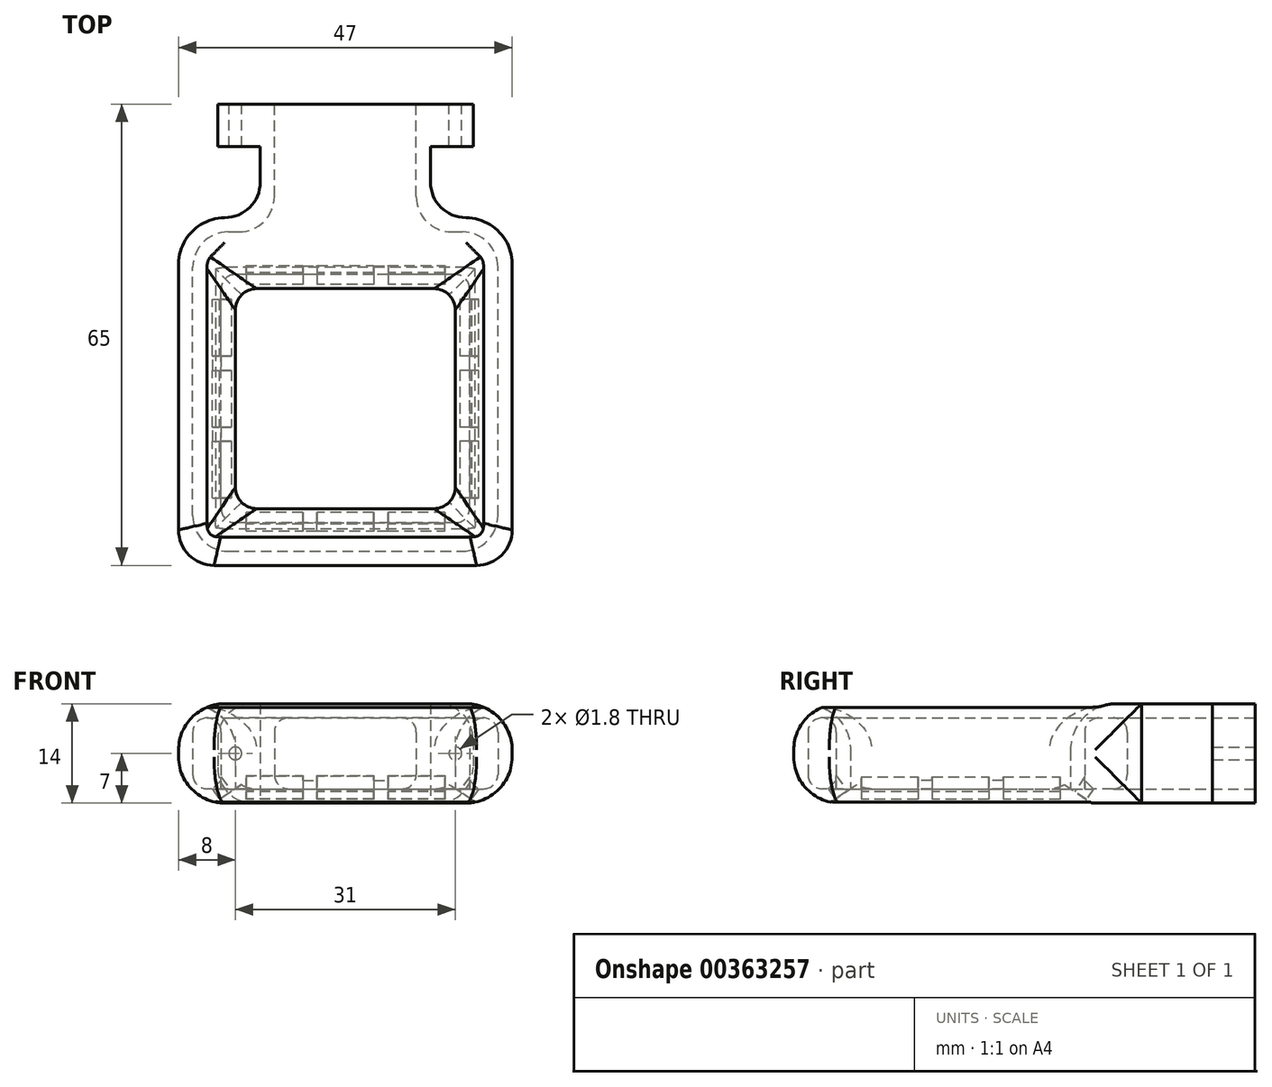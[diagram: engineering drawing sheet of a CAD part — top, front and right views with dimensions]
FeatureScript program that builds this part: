
annotation { "Feature Type Name" : "Feature", "Feature Type Description" : "" }
export const myFeature = defineFeature(function(context is Context, id is Id, definition is map)
    precondition{}
    {
        {
            var Q0;
            Q0=qCreatedBy(makeId("Top.planeOp"),FACE);
            var sketch = newSketch(context, id + "F0", { "sketchPlane" : qUnion([Q0])});
            skLineSegment(sketch, "E0.bottom", {"start": v(-12, 24.5) * mm, "end": v(12, 24.5) * mm});
            skLineSegment(sketch, "E0.top", {"start": v(-12, 40.5) * mm, "end": v(12, 40.5) * mm});
            skLineSegment(sketch, "E0.left", {"start": v(-12, 24.5) * mm, "end": v(-12, 40.5) * mm});
            skLineSegment(sketch, "E0.right", {"start": v(12, 24.5) * mm, "end": v(12, 40.5) * mm});
            skLineSegment(sketch, "E1.bottom", {"start": v(-23.5, -24.5) * mm, "end": v(23.5, -24.5) * mm});
            skLineSegment(sketch, "E1.top", {"start": v(-23.5, 24.5) * mm, "end": v(23.5, 24.5) * mm});
            skLineSegment(sketch, "E1.left", {"start": v(-23.5, -24.5) * mm, "end": v(-23.5, 24.5) * mm});
            skLineSegment(sketch, "E1.right", {"start": v(23.5, -24.5) * mm, "end": v(23.5, 24.5) * mm});
            skPoint(sketch, "E2", {"position": v(0, 24.5) * mm});
            skLineSegment(sketch, "E3.bottom", {"start": v(15.5, -16.5) * mm, "end": v(-15.5, -16.5) * mm});
            skLineSegment(sketch, "E3.top", {"start": v(15.5, 14.5) * mm, "end": v(-15.5, 14.5) * mm});
            skLineSegment(sketch, "E3.left", {"start": v(15.5, -16.5) * mm, "end": v(15.5, 14.5) * mm});
            skLineSegment(sketch, "E3.right", {"start": v(-15.5, -16.5) * mm, "end": v(-15.5, 14.5) * mm});
            skPoint(sketch, "E3.middle", {"position": v(0, 0) * mm});
            skPoint(sketch, "E4", {"position": v(-23.5, 0) * mm});
            skSolve(sketch);
        }
        {
            var Q0;
            Q0=qSketchRegion(id+"F0",true);
            extrude(context, id + "F1", {"entities" : qUnion([Q0]), "depth" : 14 * mm});
        }
        {
            var Q0;
            Q0=makeQuery(id+"F1.opExtrude","SWEPT_FACE",FACE,{"disambiguationData":[OSD([sQuery(id+"F0.wireOp",EDGE,"E0.top")])]});
            shell(context, id + "F2", {"entities" : qUnion([Q0]), "thickness" : 2 * mm});
        }
        {
            var Q0;
            Q0=makeQuery(id+"F1.opExtrude","SWEPT_FACE",FACE,{"disambiguationData":[OSD([sQuery(id+"F0.wireOp",EDGE,"E0.right")])]});
            var sketch = newSketch(context, id + "F3", { "sketchPlane" : qUnion([Q0])});
            skLineSegment(sketch, "E5.bottom", {"start": v(40.5, 14) * mm, "end": v(34.5, 14) * mm});
            skLineSegment(sketch, "E5.top", {"start": v(40.5, 0) * mm, "end": v(34.5, 0) * mm});
            skLineSegment(sketch, "E5.left", {"start": v(40.5, 14) * mm, "end": v(40.5, 0) * mm});
            skLineSegment(sketch, "E5.right", {"start": v(34.5, 14) * mm, "end": v(34.5, 0) * mm});
            skSolve(sketch);
        }
        {
            var Q0;
            Q0=makeQuery(id+"F3.imprint","IMPRINT",FACE,{"disambiguationData":[TD([[makeQuery(id+"F3.imprint","IMPRINT",EDGE,{"derivedFrom":sQuery(id+"F3.wireOp",EDGE,"E5.bottom")}),-1.0]])]});
            extrude(context, id + "F4", {"entities" : qUnion([Q0]), "operationType" : NewBodyOperationType.ADD, "depth" : 6 * mm});
        }
        {
            var Q0;
            Q0=makeQuery(id+"F1.opExtrude","SWEPT_FACE",FACE,{"disambiguationData":[OSD([sQuery(id+"F0.wireOp",EDGE,"E0.left")])]});
            var sketch = newSketch(context, id + "F5", { "sketchPlane" : qUnion([Q0])});
            skLineSegment(sketch, "E6.bottom", {"start": v(-40.5, 14) * mm, "end": v(-34.5, 14) * mm});
            skLineSegment(sketch, "E6.top", {"start": v(-40.5, 0) * mm, "end": v(-34.5, 0) * mm});
            skLineSegment(sketch, "E6.left", {"start": v(-40.5, 14) * mm, "end": v(-40.5, 0) * mm});
            skLineSegment(sketch, "E6.right", {"start": v(-34.5, 14) * mm, "end": v(-34.5, 0) * mm});
            skSolve(sketch);
        }
        {
            var Q0;
            Q0=makeQuery(id+"F5.imprint","IMPRINT",FACE,{"disambiguationData":[TD([[makeQuery(id+"F5.imprint","IMPRINT",EDGE,{"derivedFrom":sQuery(id+"F5.wireOp",EDGE,"E6.bottom")}),1.0]])]});
            extrude(context, id + "F6", {"entities" : qUnion([Q0]), "operationType" : NewBodyOperationType.ADD, "depth" : 6 * mm});
        }
        {
            var Q0;
            Q0=makeQuery(id+"F6.boolean.opBoolean","MERGE",FACE,{"derivedFrom":[makeQuery(id+"F4.boolean.opBoolean","MERGE",FACE,{"derivedFrom":[makeQuery(id+"FMbawrjq5tevXZs_1.boolean.opBoolean","MERGE",FACE,{"derivedFrom":[makeQuery(id+"F1.opExtrude","SWEPT_FACE",FACE,{"disambiguationData":[OSD([sQuery(id+"F0.wireOp",EDGE,"E0.top")])]}),makeQuery(id+"FMbawrjq5tevXZs_1.opExtrude","SWEPT_FACE",FACE,{"disambiguationData":[OSD([sQuery(id+"FMr8k5ix8z9LvOk_1.wireOp",EDGE,"X72l2WwN-p526-XuUv-XZvA-PvNH8UyjeKjB.left")])]})]}),makeQuery(id+"F4.opExtrude","SWEPT_FACE",FACE,{"disambiguationData":[OSD([sQuery(id+"F3.wireOp",EDGE,"E5.left")])]})]}),makeQuery(id+"F6.opExtrude","SWEPT_FACE",FACE,{"disambiguationData":[OSD([sQuery(id+"F5.wireOp",EDGE,"E6.left")])]})]});
            var sketch = newSketch(context, id + "F7", { "sketchPlane" : qUnion([Q0])});
            skCircle(sketch, "E7", {"center": v(-15.5, 7) * mm, "radius": 0.9 * mm});
            skCircle(sketch, "E8", {"center": v(15.5, 7) * mm, "radius": 0.9 * mm});
            skSolve(sketch);
        }
        {
            var Q0;
            Q0=makeQuery(id+"F4.opExtrude","CAP_EDGE",EDGE,{"disambiguationData":[OSD([sQuery(id+"F3.wireOp",EDGE,"E5.top")])],"isStart":false});
            var Q1;
            Q1=makeQuery(id+"F4.opExtrude","CAP_EDGE",EDGE,{"disambiguationData":[OSD([sQuery(id+"F3.wireOp",EDGE,"E5.bottom")])],"isStart":false});
            var Q2;
            Q2=makeQuery(id+"F6.opExtrude","CAP_EDGE",EDGE,{"disambiguationData":[OSD([sQuery(id+"F5.wireOp",EDGE,"E6.bottom")])],"isStart":false});
            var Q3;
            Q3=makeQuery(id+"F6.opExtrude","CAP_EDGE",EDGE,{"disambiguationData":[OSD([sQuery(id+"F5.wireOp",EDGE,"E6.top")])],"isStart":false});
            fillet(context, id + "F8", {"entities" : qUnion([Q0, Q1, Q2, Q3]), "radius" : 5 * mm, "tangentPropagation" : true, "allowEdgeOverflow" : false});
        }
        {
            var Q0;
            Q0=qSketchRegion(id+"F7",true);
            extrude(context, id + "F9", {"entities" : qUnion([Q0]), "operationType" : NewBodyOperationType.REMOVE, "endBound" : BoundingType.UP_TO_NEXT, "oppositeDirection" : true, "depth" : 25 * mm});
        }
        {
            var Q0;
            Q0=makeQuery(id+"F1.opExtrude","CAP_EDGE",EDGE,{"disambiguationData":[OSD([sQuery(id+"F0.wireOp",EDGE,"E3.right")])],"isStart":true});
            var Q1;
            Q1=makeQuery(id+"F1.opExtrude","CAP_EDGE",EDGE,{"disambiguationData":[OSD([sQuery(id+"F0.wireOp",EDGE,"E3.top")])],"isStart":true});
            var Q2;
            Q2=makeQuery(id+"F1.opExtrude","CAP_EDGE",EDGE,{"disambiguationData":[OSD([sQuery(id+"F0.wireOp",EDGE,"E3.bottom")])],"isStart":true});
            var Q3;
            Q3=makeQuery(id+"F1.opExtrude","CAP_EDGE",EDGE,{"disambiguationData":[OSD([sQuery(id+"F0.wireOp",EDGE,"E3.left")])],"isStart":true});
            chamfer(context, id + "F10", {"entities" : qUnion([Q0, Q1, Q2, Q3]), "chamferType" : ChamferType.TWO_OFFSETS, "width1" : 2 * mm, "oppositeDirection" : false, "width2" : 3 * mm, "tangentPropagation" : true});
        }
        {
            var Q0;
            Q0=makeQuery(id+"F1.opExtrude","CAP_EDGE",EDGE,{"disambiguationData":[OSD([sQuery(id+"F0.wireOp",EDGE,"E1.right")])],"isStart":false});
            var Q1;
            Q1=makeQuery(id+"F1.opExtrude","CAP_EDGE",EDGE,{"disambiguationData":[OSD([sQuery(id+"F0.wireOp",EDGE,"E1.right")])],"isStart":true});
            var Q2;
            Q2=makeQuery(id+"F1.opExtrude","SWEPT_EDGE",EDGE,{"disambiguationData":[OSD([sQuery(id+"F0.wireOp",EDGE,"E1.top"),sQuery(id+"F0.wireOp",EDGE,"E1.right")])]});
            var Q3;
            Q3=makeQuery(id+"F1.opExtrude","CAP_EDGE",EDGE,{"disambiguationData":[OSD([sQuery(id+"F0.wireOp",EDGE,"E1.bottom")])],"isStart":false});
            var Q4;
            Q4=makeQuery(id+"F1.opExtrude","CAP_EDGE",EDGE,{"disambiguationData":[OSD([sQuery(id+"F0.wireOp",EDGE,"E1.bottom")])],"isStart":true});
            var Q5;
            Q5=makeQuery(id+"F1.opExtrude","CAP_EDGE",EDGE,{"disambiguationData":[OSD([sQuery(id+"F0.wireOp",EDGE,"E1.left")])],"isStart":true});
            var Q6;
            Q6=makeQuery(id+"F1.opExtrude","CAP_EDGE",EDGE,{"disambiguationData":[OSD([sQuery(id+"F0.wireOp",EDGE,"E1.left")])],"isStart":false});
            var Q7;
            Q7=makeQuery(id+"F1.opExtrude","SWEPT_EDGE",EDGE,{"disambiguationData":[OSD([sQuery(id+"F0.wireOp",EDGE,"E1.top"),sQuery(id+"F0.wireOp",EDGE,"E1.left")])]});
            var Q8;
            Q8=makeQuery(id+"F1.opExtrude","CAP_EDGE",EDGE,{"disambiguationData":[OSD([sQuery(id+"F0.wireOp",EDGE,"E3.top")])],"isStart":false});
            var Q9;
            Q9=makeQuery(id+"F1.opExtrude","CAP_EDGE",EDGE,{"disambiguationData":[OSD([sQuery(id+"F0.wireOp",EDGE,"E3.right")])],"isStart":false});
            var Q10;
            Q10=makeQuery(id+"F1.opExtrude","CAP_EDGE",EDGE,{"disambiguationData":[OSD([sQuery(id+"F0.wireOp",EDGE,"E3.bottom")])],"isStart":false});
            var Q11;
            Q11=makeQuery(id+"F1.opExtrude","CAP_EDGE",EDGE,{"disambiguationData":[OSD([sQuery(id+"F0.wireOp",EDGE,"E3.left")])],"isStart":false});
            fillet(context, id + "F11", {"entities" : qUnion([Q0, Q1, Q2, Q3, Q4, Q5, Q6, Q7, Q8, Q9, Q10, Q11]), "radius" : 6.5 * mm, "tangentPropagation" : true, "allowEdgeOverflow" : false});
        }
        {
            var Q0;
            Q0=makeQuery(id+"F2.opShell","OFFSET_EDGE",EDGE,{"disambiguationData":[OSD([sQuery(id+"F0.wireOp",EDGE,"E1.top"),sQuery(id+"F0.wireOp",EDGE,"E1.right")])]});
            var Q1;
            Q1=makeQuery(id+"F2.opShell","OFFSET_EDGE",EDGE,{"disambiguationData":[OSD([sQuery(id+"F0.wireOp",EDGE,"E1.bottom"),sQuery(id+"F0.wireOp",EDGE,"E1.right")])]});
            var Q2;
            Q2=makeQuery(id+"F2.opShell","OFFSET_EDGE",EDGE,{"disambiguationData":[OSD([sQuery(id+"F0.wireOp",EDGE,"E1.bottom"),sQuery(id+"F0.wireOp",EDGE,"E1.left")])]});
            var Q3;
            Q3=makeQuery(id+"F2.opShell","OFFSET_EDGE",EDGE,{"disambiguationData":[OSD([sQuery(id+"F0.wireOp",EDGE,"E1.top"),sQuery(id+"F0.wireOp",EDGE,"E1.left")])]});
            var Q4;
            Q4=makeQuery(id+"F2.opShell","OFFSET_EDGE",EDGE,{"disambiguationData":[OSD([sQuery(id+"F0.wireOp",EDGE,"E0.left"),sQuery(id+"F0.wireOp",EDGE,"E1.top")])]});
            var Q5;
            Q5=makeQuery(id+"F2.opShell","OFFSET_EDGE",EDGE,{"disambiguationData":[OSD([sQuery(id+"F0.wireOp",EDGE,"E0.right"),sQuery(id+"F0.wireOp",EDGE,"E1.top")])]});
            var Q6;
            Q6=makeQuery(id+"F1.opExtrude","SWEPT_EDGE",EDGE,{"disambiguationData":[OSD([sQuery(id+"F0.wireOp",EDGE,"E0.right"),sQuery(id+"F0.wireOp",EDGE,"E1.top")])]});
            var Q7;
            Q7=makeQuery(id+"F1.opExtrude","SWEPT_EDGE",EDGE,{"disambiguationData":[OSD([sQuery(id+"F0.wireOp",EDGE,"E0.left"),sQuery(id+"F0.wireOp",EDGE,"E1.top")])]});
            var Q8;
            Q8=makeQuery(id+"F6.opExtrude","CAP_EDGE",EDGE,{"disambiguationData":[OSD([sQuery(id+"F5.wireOp",EDGE,"E6.right")])],"isStart":true});
            var Q9;
            Q9=makeQuery(id+"F4.opExtrude","CAP_EDGE",EDGE,{"disambiguationData":[OSD([sQuery(id+"F3.wireOp",EDGE,"E5.right")])],"isStart":true});
            fillet(context, id + "F12", {"entities" : qUnion([Q0, Q1, Q2, Q3, Q4, Q5, Q6, Q7, Q8, Q9]), "radius" : 5 * mm, "tangentPropagation" : true, "allowEdgeOverflow" : false});
        }
        {
            var Q0;
            Q0=makeQuery(id+"F1.opExtrude","SWEPT_EDGE",EDGE,{"disambiguationData":[OSD([sQuery(id+"F0.wireOp",EDGE,"E3.top"),sQuery(id+"F0.wireOp",EDGE,"E3.left")])]});
            var Q1;
            Q1=makeQuery(id+"F1.opExtrude","SWEPT_EDGE",EDGE,{"disambiguationData":[OSD([sQuery(id+"F0.wireOp",EDGE,"E3.bottom"),sQuery(id+"F0.wireOp",EDGE,"E3.left")])]});
            var Q2;
            Q2=makeQuery(id+"F1.opExtrude","SWEPT_EDGE",EDGE,{"disambiguationData":[OSD([sQuery(id+"F0.wireOp",EDGE,"E3.bottom"),sQuery(id+"F0.wireOp",EDGE,"E3.right")])]});
            var Q3;
            Q3=makeQuery(id+"F1.opExtrude","SWEPT_EDGE",EDGE,{"disambiguationData":[OSD([sQuery(id+"F0.wireOp",EDGE,"E3.top"),sQuery(id+"F0.wireOp",EDGE,"E3.right")])]});
            fillet(context, id + "F13", {"entities" : qUnion([Q0, Q1, Q2, Q3]), "radius" : 3 * mm, "tangentPropagation" : true, "allowEdgeOverflow" : false});
        }
        {
            var Q0;
            Q0=makeQuery(id+"F1.opExtrude","SWEPT_EDGE",EDGE,{"disambiguationData":[OSD([sQuery(id+"F0.wireOp",EDGE,"E1.bottom"),sQuery(id+"F0.wireOp",EDGE,"E1.left")])]});
            var Q1;
            Q1=makeQuery(id+"F1.opExtrude","SWEPT_EDGE",EDGE,{"disambiguationData":[OSD([sQuery(id+"F0.wireOp",EDGE,"E1.bottom"),sQuery(id+"F0.wireOp",EDGE,"E1.right")])]});
            fillet(context, id + "F14", {"entities" : qUnion([Q0, Q1]), "radius" : 5 * mm, "tangentPropagation" : true, "allowEdgeOverflow" : false});
        }
        {
            var Q0;
            Q0=makeQuery(id+"F10.opChamfer","BLEND_FACE",FACE,{"disambiguationData":[OSD([sQuery(id+"F0.wireOp",EDGE,"E3.left")])]});
            var sketch = newSketch(context, id + "F15", { "sketchPlane" : qUnion([Q0])});
            skLineSegment(sketch, "E9", {"start": v(13.5, -15.93) * mm, "end": v(13.5, 17.93) * mm, "construction": true});
            skLineSegment(sketch, "E10.bottom", {"start": v(14.5, -3) * mm, "end": v(12.5, -3) * mm});
            skLineSegment(sketch, "E10.top", {"start": v(14.5, 5) * mm, "end": v(12.5, 5) * mm});
            skLineSegment(sketch, "E10.left", {"start": v(14.5, -3) * mm, "end": v(14.5, 5) * mm});
            skLineSegment(sketch, "E10.right", {"start": v(12.5, -3) * mm, "end": v(12.5, 5) * mm});
            skPoint(sketch, "E10.middle", {"position": v(13.5, 1) * mm});
            skLineSegment(sketch, "E11.bottom", {"start": v(14.5, -13) * mm, "end": v(12.5, -13) * mm});
            skLineSegment(sketch, "E11.top", {"start": v(14.5, -5) * mm, "end": v(12.5, -5) * mm});
            skLineSegment(sketch, "E11.left", {"start": v(14.5, -13) * mm, "end": v(14.5, -5) * mm});
            skLineSegment(sketch, "E11.right", {"start": v(12.5, -13) * mm, "end": v(12.5, -5) * mm});
            skPoint(sketch, "E11.middle", {"position": v(13.5, -9) * mm});
            skLineSegment(sketch, "E12.bottom", {"start": v(14.5, 7) * mm, "end": v(12.5, 7) * mm});
            skLineSegment(sketch, "E12.top", {"start": v(14.5, 15) * mm, "end": v(12.5, 15) * mm});
            skLineSegment(sketch, "E12.left", {"start": v(14.5, 7) * mm, "end": v(14.5, 15) * mm});
            skLineSegment(sketch, "E12.right", {"start": v(12.5, 7) * mm, "end": v(12.5, 15) * mm});
            skPoint(sketch, "E12.middle", {"position": v(13.5, 11) * mm});
            skSolve(sketch);
        }
        {
            var Q0;
            Q0=makeQuery(id+"F15.imprint","IMPRINT",FACE,{"disambiguationData":[TD([[makeQuery(id+"F15.imprint","IMPRINT",EDGE,{"derivedFrom":sQuery(id+"F15.wireOp",EDGE,"E11.bottom")}),-1.0]])]});
            var Q1;
            Q1=makeQuery(id+"F15.imprint","IMPRINT",FACE,{"disambiguationData":[TD([[makeQuery(id+"F15.imprint","IMPRINT",EDGE,{"derivedFrom":sQuery(id+"F15.wireOp",EDGE,"E10.bottom")}),-1.0]])]});
            var Q2;
            Q2=makeQuery(id+"F15.imprint","IMPRINT",FACE,{"disambiguationData":[TD([[makeQuery(id+"F15.imprint","IMPRINT",EDGE,{"derivedFrom":sQuery(id+"F15.wireOp",EDGE,"E12.bottom")}),-1.0]])]});
            extrude(context, id + "F16", {"entities" : qUnion([Q0, Q1, Q2]), "operationType" : NewBodyOperationType.REMOVE, "oppositeDirection" : true, "depth" : 3 * mm});
        }
        {
            var Q0;
            Q0=makeQuery(id+"F10.opChamfer","BLEND_FACE",FACE,{"disambiguationData":[OSD([sQuery(id+"F0.wireOp",EDGE,"E3.right")])]});
            var sketch = newSketch(context, id + "F17", { "sketchPlane" : qUnion([Q0])});
            skLineSegment(sketch, "E13", {"start": v(-13.5, -15.93) * mm, "end": v(-13.5, 17.93) * mm, "construction": true});
            skLineSegment(sketch, "E14.bottom", {"start": v(-12.5, -3) * mm, "end": v(-14.5, -3) * mm});
            skLineSegment(sketch, "E14.top", {"start": v(-12.5, 5) * mm, "end": v(-14.5, 5) * mm});
            skLineSegment(sketch, "E14.left", {"start": v(-12.5, -3) * mm, "end": v(-12.5, 5) * mm});
            skLineSegment(sketch, "E14.right", {"start": v(-14.5, -3) * mm, "end": v(-14.5, 5) * mm});
            skPoint(sketch, "E14.middle", {"position": v(-13.5, 1) * mm});
            skLineSegment(sketch, "E15.bottom", {"start": v(-12.5, -13) * mm, "end": v(-14.5, -13) * mm});
            skLineSegment(sketch, "E15.top", {"start": v(-12.5, -5) * mm, "end": v(-14.5, -5) * mm});
            skLineSegment(sketch, "E15.left", {"start": v(-12.5, -13) * mm, "end": v(-12.5, -5) * mm});
            skLineSegment(sketch, "E15.right", {"start": v(-14.5, -13) * mm, "end": v(-14.5, -5) * mm});
            skPoint(sketch, "E15.middle", {"position": v(-13.5, -9) * mm});
            skLineSegment(sketch, "E16.bottom", {"start": v(-12.5, 7) * mm, "end": v(-14.5, 7) * mm});
            skLineSegment(sketch, "E16.top", {"start": v(-12.5, 15) * mm, "end": v(-14.5, 15) * mm});
            skLineSegment(sketch, "E16.left", {"start": v(-12.5, 7) * mm, "end": v(-12.5, 15) * mm});
            skLineSegment(sketch, "E16.right", {"start": v(-14.5, 7) * mm, "end": v(-14.5, 15) * mm});
            skPoint(sketch, "E16.middle", {"position": v(-13.5, 11) * mm});
            skSolve(sketch);
        }
        {
            var Q0;
            Q0=makeQuery(id+"F10.opChamfer","BLEND_FACE",FACE,{"disambiguationData":[OSD([sQuery(id+"F0.wireOp",EDGE,"E3.top")])]});
            var sketch = newSketch(context, id + "F18", { "sketchPlane" : qUnion([Q0])});
            skLineSegment(sketch, "E17", {"start": v(-16.91, -12.65) * mm, "end": v(16.91, -12.65) * mm, "construction": true});
            skLineSegment(sketch, "E18.bottom", {"start": v(4, -13.65) * mm, "end": v(-4, -13.65) * mm});
            skLineSegment(sketch, "E18.top", {"start": v(4, -11.65) * mm, "end": v(-4, -11.65) * mm});
            skLineSegment(sketch, "E18.left", {"start": v(4, -13.65) * mm, "end": v(4, -11.65) * mm});
            skLineSegment(sketch, "E18.right", {"start": v(-4, -13.65) * mm, "end": v(-4, -11.65) * mm});
            skPoint(sketch, "E18.middle", {"position": v(0, -12.65) * mm});
            skLineSegment(sketch, "E19.bottom", {"start": v(-6, -13.65) * mm, "end": v(-14, -13.65) * mm});
            skLineSegment(sketch, "E19.top", {"start": v(-6, -11.65) * mm, "end": v(-14, -11.65) * mm});
            skLineSegment(sketch, "E19.left", {"start": v(-6, -13.65) * mm, "end": v(-6, -11.65) * mm});
            skLineSegment(sketch, "E19.right", {"start": v(-14, -13.65) * mm, "end": v(-14, -11.65) * mm});
            skPoint(sketch, "E19.middle", {"position": v(-10, -12.65) * mm});
            skLineSegment(sketch, "E20.bottom", {"start": v(14, -13.65) * mm, "end": v(6, -13.65) * mm});
            skLineSegment(sketch, "E20.top", {"start": v(14, -11.65) * mm, "end": v(6, -11.65) * mm});
            skLineSegment(sketch, "E20.left", {"start": v(14, -13.65) * mm, "end": v(14, -11.65) * mm});
            skLineSegment(sketch, "E20.right", {"start": v(6, -13.65) * mm, "end": v(6, -11.65) * mm});
            skPoint(sketch, "E20.middle", {"position": v(10, -12.65) * mm});
            skSolve(sketch);
        }
        {
            var Q0;
            Q0=makeQuery(id+"F10.opChamfer","BLEND_FACE",FACE,{"disambiguationData":[OSD([sQuery(id+"F0.wireOp",EDGE,"E3.bottom")])]});
            var sketch = newSketch(context, id + "F19", { "sketchPlane" : qUnion([Q0])});
            skLineSegment(sketch, "E21", {"start": v(-16.91, 14.23) * mm, "end": v(16.91, 14.23) * mm, "construction": true});
            skLineSegment(sketch, "E22.bottom", {"start": v(4, 13.23) * mm, "end": v(-4, 13.23) * mm});
            skLineSegment(sketch, "E22.top", {"start": v(4, 15.23) * mm, "end": v(-4, 15.23) * mm});
            skLineSegment(sketch, "E22.left", {"start": v(4, 13.23) * mm, "end": v(4, 15.23) * mm});
            skLineSegment(sketch, "E22.right", {"start": v(-4, 13.23) * mm, "end": v(-4, 15.23) * mm});
            skPoint(sketch, "E22.middle", {"position": v(0, 14.23) * mm});
            skLineSegment(sketch, "E23.bottom", {"start": v(-6, 13.23) * mm, "end": v(-14, 13.23) * mm});
            skLineSegment(sketch, "E23.top", {"start": v(-6, 15.23) * mm, "end": v(-14, 15.23) * mm});
            skLineSegment(sketch, "E23.left", {"start": v(-6, 13.23) * mm, "end": v(-6, 15.23) * mm});
            skLineSegment(sketch, "E23.right", {"start": v(-14, 13.23) * mm, "end": v(-14, 15.23) * mm});
            skPoint(sketch, "E23.middle", {"position": v(-10, 14.23) * mm});
            skLineSegment(sketch, "E24.bottom", {"start": v(14, 13.23) * mm, "end": v(6, 13.23) * mm});
            skLineSegment(sketch, "E24.top", {"start": v(14, 15.23) * mm, "end": v(6, 15.23) * mm});
            skLineSegment(sketch, "E24.left", {"start": v(14, 13.23) * mm, "end": v(14, 15.23) * mm});
            skLineSegment(sketch, "E24.right", {"start": v(6, 13.23) * mm, "end": v(6, 15.23) * mm});
            skPoint(sketch, "E24.middle", {"position": v(10, 14.23) * mm});
            skSolve(sketch);
        }
        {
            var Q0;
            Q0=makeQuery(id+"F17.imprint","IMPRINT",FACE,{"disambiguationData":[TD([[makeQuery(id+"F17.imprint","IMPRINT",EDGE,{"derivedFrom":sQuery(id+"F17.wireOp",EDGE,"E16.bottom")}),-1.0]])]});
            var Q1;
            Q1=makeQuery(id+"F17.imprint","IMPRINT",FACE,{"disambiguationData":[TD([[makeQuery(id+"F17.imprint","IMPRINT",EDGE,{"derivedFrom":sQuery(id+"F17.wireOp",EDGE,"E14.bottom")}),-1.0]])]});
            var Q2;
            Q2=makeQuery(id+"F17.imprint","IMPRINT",FACE,{"disambiguationData":[TD([[makeQuery(id+"F17.imprint","IMPRINT",EDGE,{"derivedFrom":sQuery(id+"F17.wireOp",EDGE,"E15.bottom")}),-1.0]])]});
            extrude(context, id + "F20", {"entities" : qUnion([Q0, Q1, Q2]), "operationType" : NewBodyOperationType.REMOVE, "oppositeDirection" : true, "depth" : 3 * mm});
        }
        {
            var Q0;
            Q0=makeQuery(id+"F19.imprint","IMPRINT",FACE,{"disambiguationData":[TD([[makeQuery(id+"F19.imprint","IMPRINT",EDGE,{"derivedFrom":sQuery(id+"F19.wireOp",EDGE,"E23.bottom")}),-1.0]])]});
            var Q1;
            Q1=makeQuery(id+"F19.imprint","IMPRINT",FACE,{"disambiguationData":[TD([[makeQuery(id+"F19.imprint","IMPRINT",EDGE,{"derivedFrom":sQuery(id+"F19.wireOp",EDGE,"E22.bottom")}),-1.0]])]});
            var Q2;
            Q2=makeQuery(id+"F19.imprint","IMPRINT",FACE,{"disambiguationData":[TD([[makeQuery(id+"F19.imprint","IMPRINT",EDGE,{"derivedFrom":sQuery(id+"F19.wireOp",EDGE,"E24.bottom")}),-1.0]])]});
            extrude(context, id + "F21", {"entities" : qUnion([Q0, Q1, Q2]), "operationType" : NewBodyOperationType.REMOVE, "oppositeDirection" : true, "depth" : 3 * mm});
        }
        {
            var Q0;
            Q0=makeQuery(id+"F18.imprint","IMPRINT",FACE,{"disambiguationData":[TD([[makeQuery(id+"F18.imprint","IMPRINT",EDGE,{"derivedFrom":sQuery(id+"F18.wireOp",EDGE,"E19.bottom")}),-1.0]])]});
            var Q1;
            Q1=makeQuery(id+"F18.imprint","IMPRINT",FACE,{"disambiguationData":[TD([[makeQuery(id+"F18.imprint","IMPRINT",EDGE,{"derivedFrom":sQuery(id+"F18.wireOp",EDGE,"E18.bottom")}),-1.0]])]});
            var Q2;
            Q2=makeQuery(id+"F18.imprint","IMPRINT",FACE,{"disambiguationData":[TD([[makeQuery(id+"F18.imprint","IMPRINT",EDGE,{"derivedFrom":sQuery(id+"F18.wireOp",EDGE,"E20.bottom")}),-1.0]])]});
            extrude(context, id + "F22", {"entities" : qUnion([Q0, Q1, Q2]), "operationType" : NewBodyOperationType.REMOVE, "oppositeDirection" : true, "depth" : 3 * mm});
        }
        {
            var Q0;
            {var subQ2=sQuery(id+"F0.wireOp",EDGE,"E3.top");Q0=makeQuery(id+"F22.boolean.opBoolean","SPLIT",EDGE,{"disambiguationData":[TD([makeQuery(id+"F22.opExtrude","SWEPT_FACE",FACE,{"disambiguationData":[OSD([sQuery(id+"F18.wireOp",EDGE,"E18.right")])]})])],"derivedFrom":makeQuery(id+"F2.opShell","OFFSET_EDGE",EDGE,{"disambiguationData":[OSD([subQ2]),TDD([makeQuery(id+"F1.opExtrude","CAP_EDGE",EDGE,{"disambiguationData":[OSD([subQ2])],"isStart":true})])]})});}
            var Q1;
            {var subQ2=sQuery(id+"F0.wireOp",EDGE,"E3.top");Q1=makeQuery(id+"F22.boolean.opBoolean","SPLIT",EDGE,{"disambiguationData":[TD([makeQuery(id+"F22.opExtrude","SWEPT_FACE",FACE,{"disambiguationData":[OSD([sQuery(id+"F18.wireOp",EDGE,"E18.left")])]})])],"derivedFrom":makeQuery(id+"F2.opShell","OFFSET_EDGE",EDGE,{"disambiguationData":[OSD([subQ2]),TDD([makeQuery(id+"F1.opExtrude","CAP_EDGE",EDGE,{"disambiguationData":[OSD([subQ2])],"isStart":true})])]})});}
            var Q2;
            {var subQ0=sQuery(id+"F0.wireOp",EDGE,"E3.right");Q2=makeQuery(id+"F20.boolean.opBoolean","SPLIT",EDGE,{"disambiguationData":[TD([makeQuery(id+"F20.opExtrude","SWEPT_FACE",FACE,{"disambiguationData":[OSD([sQuery(id+"F17.wireOp",EDGE,"E14.top")])]})])],"derivedFrom":makeQuery(id+"F2.opShell","OFFSET_EDGE",EDGE,{"disambiguationData":[OSD([subQ0]),TDD([makeQuery(id+"F1.opExtrude","CAP_EDGE",EDGE,{"disambiguationData":[OSD([subQ0])],"isStart":true})])]})});}
            var Q3;
            {var subQ0=sQuery(id+"F0.wireOp",EDGE,"E3.right");Q3=makeQuery(id+"F20.boolean.opBoolean","SPLIT",EDGE,{"disambiguationData":[TD([makeQuery(id+"F20.opExtrude","SWEPT_FACE",FACE,{"disambiguationData":[OSD([sQuery(id+"F17.wireOp",EDGE,"E14.bottom")])]})])],"derivedFrom":makeQuery(id+"F2.opShell","OFFSET_EDGE",EDGE,{"disambiguationData":[OSD([subQ0]),TDD([makeQuery(id+"F1.opExtrude","CAP_EDGE",EDGE,{"disambiguationData":[OSD([subQ0])],"isStart":true})])]})});}
            var Q4;
            {var subQ3=sQuery(id+"F0.wireOp",EDGE,"E3.bottom");Q4=makeQuery(id+"F21.boolean.opBoolean","SPLIT",EDGE,{"disambiguationData":[TD([makeQuery(id+"F21.opExtrude","SWEPT_FACE",FACE,{"disambiguationData":[OSD([sQuery(id+"F19.wireOp",EDGE,"E22.right")])]})])],"derivedFrom":makeQuery(id+"F2.opShell","OFFSET_EDGE",EDGE,{"disambiguationData":[OSD([subQ3]),TDD([makeQuery(id+"F1.opExtrude","CAP_EDGE",EDGE,{"disambiguationData":[OSD([subQ3])],"isStart":true})])]})});}
            var Q5;
            {var subQ3=sQuery(id+"F0.wireOp",EDGE,"E3.bottom");Q5=makeQuery(id+"F21.boolean.opBoolean","SPLIT",EDGE,{"disambiguationData":[TD([makeQuery(id+"F21.opExtrude","SWEPT_FACE",FACE,{"disambiguationData":[OSD([sQuery(id+"F19.wireOp",EDGE,"E22.left")])]})])],"derivedFrom":makeQuery(id+"F2.opShell","OFFSET_EDGE",EDGE,{"disambiguationData":[OSD([subQ3]),TDD([makeQuery(id+"F1.opExtrude","CAP_EDGE",EDGE,{"disambiguationData":[OSD([subQ3])],"isStart":true})])]})});}
            var Q6;
            {var subQ1=sQuery(id+"F0.wireOp",EDGE,"E3.left");Q6=makeQuery(id+"F16.boolean.opBoolean","SPLIT",EDGE,{"disambiguationData":[TD([makeQuery(id+"F16.opExtrude","SWEPT_FACE",FACE,{"disambiguationData":[OSD([sQuery(id+"F15.wireOp",EDGE,"E10.top")])]})])],"derivedFrom":makeQuery(id+"F2.opShell","OFFSET_EDGE",EDGE,{"disambiguationData":[OSD([subQ1]),TDD([makeQuery(id+"F1.opExtrude","CAP_EDGE",EDGE,{"disambiguationData":[OSD([subQ1])],"isStart":true})])]})});}
            var Q7;
            {var subQ1=sQuery(id+"F0.wireOp",EDGE,"E3.left");Q7=makeQuery(id+"F16.boolean.opBoolean","SPLIT",EDGE,{"disambiguationData":[TD([makeQuery(id+"F16.opExtrude","SWEPT_FACE",FACE,{"disambiguationData":[OSD([sQuery(id+"F15.wireOp",EDGE,"E10.bottom")])]})])],"derivedFrom":makeQuery(id+"F2.opShell","OFFSET_EDGE",EDGE,{"disambiguationData":[OSD([subQ1]),TDD([makeQuery(id+"F1.opExtrude","CAP_EDGE",EDGE,{"disambiguationData":[OSD([subQ1])],"isStart":true})])]})});}
            chamfer(context, id + "F23", {"entities" : qUnion([Q0, Q1, Q2, Q3, Q4, Q5, Q6, Q7]), "width" : 1.2 * mm, "tangentPropagation" : true});
        }
        {
            var Q0;
            Q0=makeQuery(id+"F2.opShell","OFFSET_EDGE",EDGE,{"disambiguationData":[OSD([sQuery(id+"F0.wireOp",EDGE,"E3.top"),sQuery(id+"F0.wireOp",EDGE,"E3.left")])]});
            var Q1;
            Q1=makeQuery(id+"F2.opShell","OFFSET_EDGE",EDGE,{"disambiguationData":[OSD([sQuery(id+"F0.wireOp",EDGE,"E3.top"),sQuery(id+"F0.wireOp",EDGE,"E3.right")])]});
            var Q2;
            Q2=makeQuery(id+"F2.opShell","OFFSET_EDGE",EDGE,{"disambiguationData":[OSD([sQuery(id+"F0.wireOp",EDGE,"E3.bottom"),sQuery(id+"F0.wireOp",EDGE,"E3.left")])]});
            var Q3;
            Q3=makeQuery(id+"F2.opShell","OFFSET_EDGE",EDGE,{"disambiguationData":[OSD([sQuery(id+"F0.wireOp",EDGE,"E3.bottom"),sQuery(id+"F0.wireOp",EDGE,"E3.right")])]});
            fillet(context, id + "F24", {"entities" : qUnion([Q0, Q1, Q2, Q3]), "radius" : 2 * mm, "tangentPropagation" : true, "allowEdgeOverflow" : false});
        }
        {
            var Q0;
            {var subQ0=sQuery(id+"F0.wireOp",EDGE,"E3.right");var subQ1=sQuery(id+"F0.wireOp",EDGE,"E3.left");var subQ2=sQuery(id+"F0.wireOp",EDGE,"E3.top");var subQ3=sQuery(id+"F0.wireOp",EDGE,"E3.bottom");var subQ4=sQuery(id+"F0.wireOp",EDGE,"E1.right");var subQ5=sQuery(id+"F0.wireOp",EDGE,"E1.left");var subQ6=sQuery(id+"F0.wireOp",EDGE,"E1.top");var subQ7=sQuery(id+"F0.wireOp",EDGE,"E1.bottom");var subQ8=sQuery(id+"F0.wireOp",EDGE,"E0.right");var subQ9=sQuery(id+"F0.wireOp",EDGE,"E0.left");var subQ10=sQuery(id+"F0.wireOp",EDGE,"E0.top");Q0=makeQuery(id+"F12.opFillet","BLEND_EDGE",EDGE,{"blendedFrom":[makeQuery(id+"F2.opShell","OFFSET_EDGE",EDGE,{"disambiguationData":[OSD([subQ6,subQ4])]}),makeQuery(id+"F2.opShell","OFFSET_FACE",FACE,{"disambiguationData":[OSD([subQ10,subQ9,subQ8,subQ7,subQ6,subQ5,subQ4,subQ3,subQ2,subQ1,subQ0]),TDD([makeQuery(id+"F1.opExtrude","CAP_FACE",FACE,{"disambiguationData":[OSD([subQ10,subQ9,subQ8,subQ7,subQ6,subQ5,subQ4,subQ3,subQ2,subQ1,subQ0])],"isStart":false})])]})],"blendedInto":[makeQuery(id+"F2.opShell","OFFSET_FACE",FACE,{"disambiguationData":[OSD([subQ10,subQ9,subQ8,subQ7,subQ6,subQ5,subQ4,subQ3,subQ2,subQ1,subQ0]),TDD([makeQuery(id+"F1.opExtrude","CAP_FACE",FACE,{"disambiguationData":[OSD([subQ10,subQ9,subQ8,subQ7,subQ6,subQ5,subQ4,subQ3,subQ2,subQ1,subQ0])],"isStart":false})])]})]});}
            var Q1;
            {var subQ0=sQuery(id+"F0.wireOp",EDGE,"E3.right");var subQ1=sQuery(id+"F0.wireOp",EDGE,"E3.left");var subQ2=sQuery(id+"F0.wireOp",EDGE,"E3.top");var subQ3=sQuery(id+"F0.wireOp",EDGE,"E3.bottom");var subQ4=sQuery(id+"F0.wireOp",EDGE,"E1.right");var subQ5=sQuery(id+"F0.wireOp",EDGE,"E1.left");var subQ6=sQuery(id+"F0.wireOp",EDGE,"E1.top");var subQ7=sQuery(id+"F0.wireOp",EDGE,"E1.bottom");var subQ8=sQuery(id+"F0.wireOp",EDGE,"E0.right");var subQ9=sQuery(id+"F0.wireOp",EDGE,"E0.left");var subQ10=sQuery(id+"F0.wireOp",EDGE,"E0.top");Q1=makeQuery(id+"F24.opFillet","BLEND_EDGE",EDGE,{"blendedFrom":[makeQuery(id+"F2.opShell","OFFSET_EDGE",EDGE,{"disambiguationData":[OSD([subQ3,subQ1])]}),makeQuery(id+"F2.opShell","OFFSET_FACE",FACE,{"disambiguationData":[OSD([subQ10,subQ9,subQ8,subQ7,subQ6,subQ5,subQ4,subQ3,subQ2,subQ1,subQ0]),TDD([makeQuery(id+"F1.opExtrude","CAP_FACE",FACE,{"disambiguationData":[OSD([subQ10,subQ9,subQ8,subQ7,subQ6,subQ5,subQ4,subQ3,subQ2,subQ1,subQ0])],"isStart":false})])]})],"blendedInto":[makeQuery(id+"F2.opShell","OFFSET_FACE",FACE,{"disambiguationData":[OSD([subQ10,subQ9,subQ8,subQ7,subQ6,subQ5,subQ4,subQ3,subQ2,subQ1,subQ0]),TDD([makeQuery(id+"F1.opExtrude","CAP_FACE",FACE,{"disambiguationData":[OSD([subQ10,subQ9,subQ8,subQ7,subQ6,subQ5,subQ4,subQ3,subQ2,subQ1,subQ0])],"isStart":false})])]})]});}
            fillet(context, id + "F25", {"entities" : qUnion([Q0, Q1]), "radius" : 2 * mm, "tangentPropagation" : true, "allowEdgeOverflow" : false});
        }
        {
            var Q0;
            {var subQ0=sQuery(id+"F0.wireOp",EDGE,"E0.right");Q0=makeQuery(id+"F2.opShell","OFFSET_EDGE",EDGE,{"disambiguationData":[OSD([subQ0]),TDD([makeQuery(id+"F1.opExtrude","CAP_EDGE",EDGE,{"disambiguationData":[OSD([subQ0])],"isStart":true})])]});}
            fillet(context, id + "F26", {"entities" : qUnion([Q0]), "radius" : 2 * mm, "tangentPropagation" : true, "allowEdgeOverflow" : false});
        }
    });
